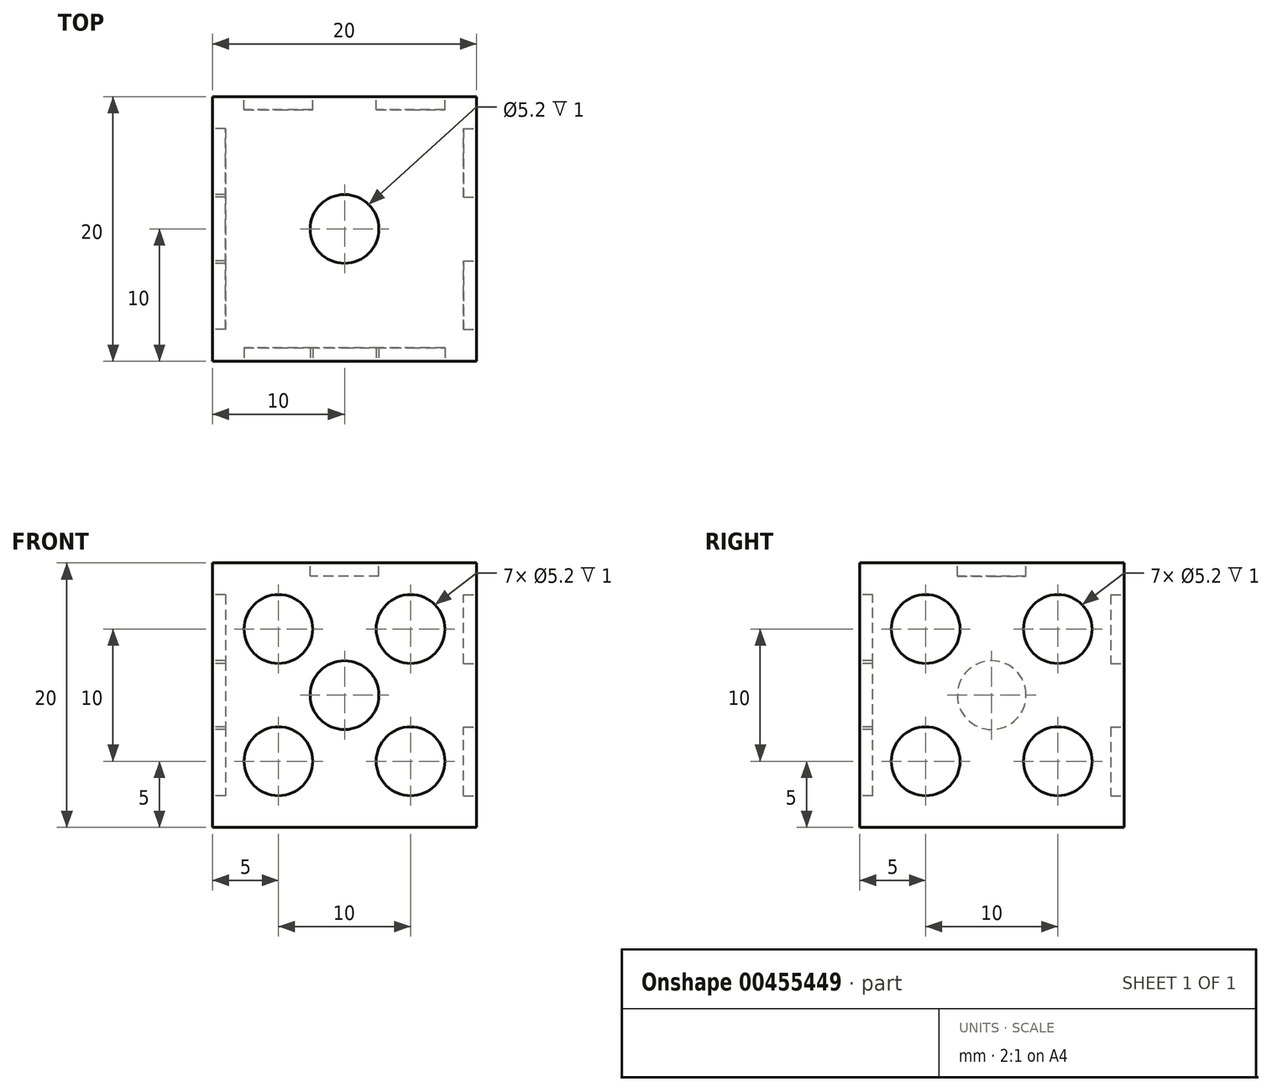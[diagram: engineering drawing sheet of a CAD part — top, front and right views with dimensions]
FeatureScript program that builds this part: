
annotation { "Feature Type Name" : "Feature", "Feature Type Description" : "" }
export const myFeature = defineFeature(function(context is Context, id is Id, definition is map)
    precondition{}
    {
        {
            var Q0;
            Q0=qCreatedBy(makeId("Front.planeOp"),FACE);
            var sketch = newSketch(context, id + "F0", { "sketchPlane" : qUnion([Q0])});
            skLineSegment(sketch, "E0.bottom", {"start": v(0, 0) * mm, "end": v(-20, 0) * mm});
            skLineSegment(sketch, "E0.top", {"start": v(0, 20) * mm, "end": v(-20, 20) * mm});
            skLineSegment(sketch, "E0.left", {"start": v(0, 0) * mm, "end": v(0, 20) * mm});
            skLineSegment(sketch, "E0.right", {"start": v(-20, 0) * mm, "end": v(-20, 20) * mm});
            skSolve(sketch);
        }
        {
            var Q0;
            Q0=makeQuery(id+"F0.imprint","IMPRINT",FACE,{"disambiguationData":[TD([[makeQuery(id+"F0.imprint","IMPRINT",EDGE,{"derivedFrom":sQuery(id+"F0.wireOp",EDGE,"E0.bottom")}),-1.0]])]});
            extrude(context, id + "F1", {"entities" : qUnion([Q0]), "depth" : 20 * mm});
        }
        {
            var Q0;
            Q0=makeQuery(id+"F1.opExtrude","CAP_FACE",FACE,{"disambiguationData":[OSD([sQuery(id+"F0.wireOp",EDGE,"E0.bottom"),sQuery(id+"F0.wireOp",EDGE,"E0.top"),sQuery(id+"F0.wireOp",EDGE,"E0.left"),sQuery(id+"F0.wireOp",EDGE,"E0.right")])],"isStart":false});
            var sketch = newSketch(context, id + "F2", { "sketchPlane" : qUnion([Q0])});
            skLineSegment(sketch, "E1", {"start": v(-10, 20) * mm, "end": v(-10, 0) * mm, "construction": true});
            skLineSegment(sketch, "E2", {"start": v(-20, 20) * mm, "end": v(0, 0) * mm, "construction": true});
            skLineSegment(sketch, "E3", {"start": v(0, 20) * mm, "end": v(-20, 0) * mm, "construction": true});
            skLineSegment(sketch, "E4", {"start": v(-20, 10) * mm, "end": v(0, 10) * mm, "construction": true});
            skCircle(sketch, "E5", {"center": v(-15, 15) * mm, "radius": 2.6 * mm});
            skCircle(sketch, "E6", {"center": v(-10, 10) * mm, "radius": 2.6 * mm});
            skCircle(sketch, "E7", {"center": v(-15, 5) * mm, "radius": 2.6 * mm});
            skCircle(sketch, "E8", {"center": v(-5, 15) * mm, "radius": 2.6 * mm});
            skCircle(sketch, "E9", {"center": v(-5, 5) * mm, "radius": 2.6 * mm});
            skSolve(sketch);
        }
        {
            var Q0;
            Q0 = qSketchRegion(id + "F2", true);
            extrude(context, id + "F3", {"entities" : qUnion([Q0]), "operationType" : NewBodyOperationType.REMOVE, "oppositeDirection" : true, "depth" : 1 * mm});
        }
        {
            var Q0;
            Q0=makeQuery(id+"F1.opExtrude","CAP_FACE",FACE,{"disambiguationData":[OSD([sQuery(id+"F0.wireOp",EDGE,"E0.bottom"),sQuery(id+"F0.wireOp",EDGE,"E0.top"),sQuery(id+"F0.wireOp",EDGE,"E0.left"),sQuery(id+"F0.wireOp",EDGE,"E0.right")])],"isStart":true});
            var sketch = newSketch(context, id + "F4", { "sketchPlane" : qUnion([Q0])});
            skLineSegment(sketch, "E10", {"start": v(20, 20) * mm, "end": v(0, 0) * mm, "construction": true});
            skCircle(sketch, "E11", {"center": v(15, 15) * mm, "radius": 2.6 * mm});
            skCircle(sketch, "E12", {"center": v(5, 5) * mm, "radius": 2.6 * mm});
            skSolve(sketch);
        }
        {
            var Q0;
            Q0 = qSketchRegion(id + "F4", true);
            extrude(context, id + "F5", {"entities" : qUnion([Q0]), "operationType" : NewBodyOperationType.REMOVE, "oppositeDirection" : true, "depth" : 1 * mm});
        }
        {
            var Q0;
            Q0=makeQuery(id+"F1.opExtrude","SWEPT_FACE",FACE,{"disambiguationData":[OSD([sQuery(id+"F0.wireOp",EDGE,"E0.top")])]});
            var sketch = newSketch(context, id + "F6", { "sketchPlane" : qUnion([Q0])});
            skLineSegment(sketch, "E13", {"start": v(-10, 0) * mm, "end": v(-10, -20) * mm, "construction": true});
            skLineSegment(sketch, "E14", {"start": v(-20, -10) * mm, "end": v(0, -10) * mm, "construction": true});
            skCircle(sketch, "E15", {"center": v(-10, -10) * mm, "radius": 2.6 * mm});
            skSolve(sketch);
        }
        {
            var Q0;
            Q0 = qSketchRegion(id + "F6", true);
            extrude(context, id + "F7", {"entities" : qUnion([Q0]), "operationType" : NewBodyOperationType.REMOVE, "oppositeDirection" : true, "depth" : 1 * mm});
        }
        {
            var Q0;
            Q0=makeQuery(id+"F1.opExtrude","SWEPT_FACE",FACE,{"disambiguationData":[OSD([sQuery(id+"F0.wireOp",EDGE,"E0.right")])]});
            var sketch = newSketch(context, id + "F8", { "sketchPlane" : qUnion([Q0])});
            skLineSegment(sketch, "E16", {"start": v(20, 20) * mm, "end": v(0, 0) * mm, "construction": true});
            skCircle(sketch, "E17", {"center": v(10, 10) * mm, "radius": 2.6 * mm});
            skCircle(sketch, "E18", {"center": v(15, 15) * mm, "radius": 2.6 * mm});
            skCircle(sketch, "E19", {"center": v(5, 5) * mm, "radius": 2.6 * mm});
            skSolve(sketch);
        }
        {
            var Q0;
            Q0 = qSketchRegion(id + "F8", true);
            extrude(context, id + "F9", {"entities" : qUnion([Q0]), "operationType" : NewBodyOperationType.REMOVE, "oppositeDirection" : true, "depth" : 1 * mm});
        }
        {
            var Q0;
            Q0=makeQuery(id+"F1.opExtrude","SWEPT_FACE",FACE,{"disambiguationData":[OSD([sQuery(id+"F0.wireOp",EDGE,"E0.left")])]});
            var sketch = newSketch(context, id + "F10", { "sketchPlane" : qUnion([Q0])});
            skLineSegment(sketch, "E20", {"start": v(-20, 20) * mm, "end": v(0, 0) * mm, "construction": true});
            skLineSegment(sketch, "E21", {"start": v(0, 20) * mm, "end": v(-20, 0) * mm, "construction": true});
            skLineSegment(sketch, "E22", {"start": v(-20, 10) * mm, "end": v(0, 10) * mm, "construction": true});
            skLineSegment(sketch, "E23", {"start": v(-10, 20) * mm, "end": v(-10, 0) * mm, "construction": true});
            skCircle(sketch, "E24", {"center": v(-15, 15) * mm, "radius": 2.6 * mm});
            skCircle(sketch, "E25", {"center": v(-15, 5) * mm, "radius": 2.6 * mm});
            skCircle(sketch, "E26", {"center": v(-5, 15) * mm, "radius": 2.6 * mm});
            skCircle(sketch, "E27", {"center": v(-5, 5) * mm, "radius": 2.6 * mm});
            skSolve(sketch);
        }
        {
            var Q0;
            Q0 = qSketchRegion(id + "F10", true);
            extrude(context, id + "F11", {"entities" : qUnion([Q0]), "operationType" : NewBodyOperationType.REMOVE, "oppositeDirection" : true, "depth" : 1 * mm});
        }
    });
